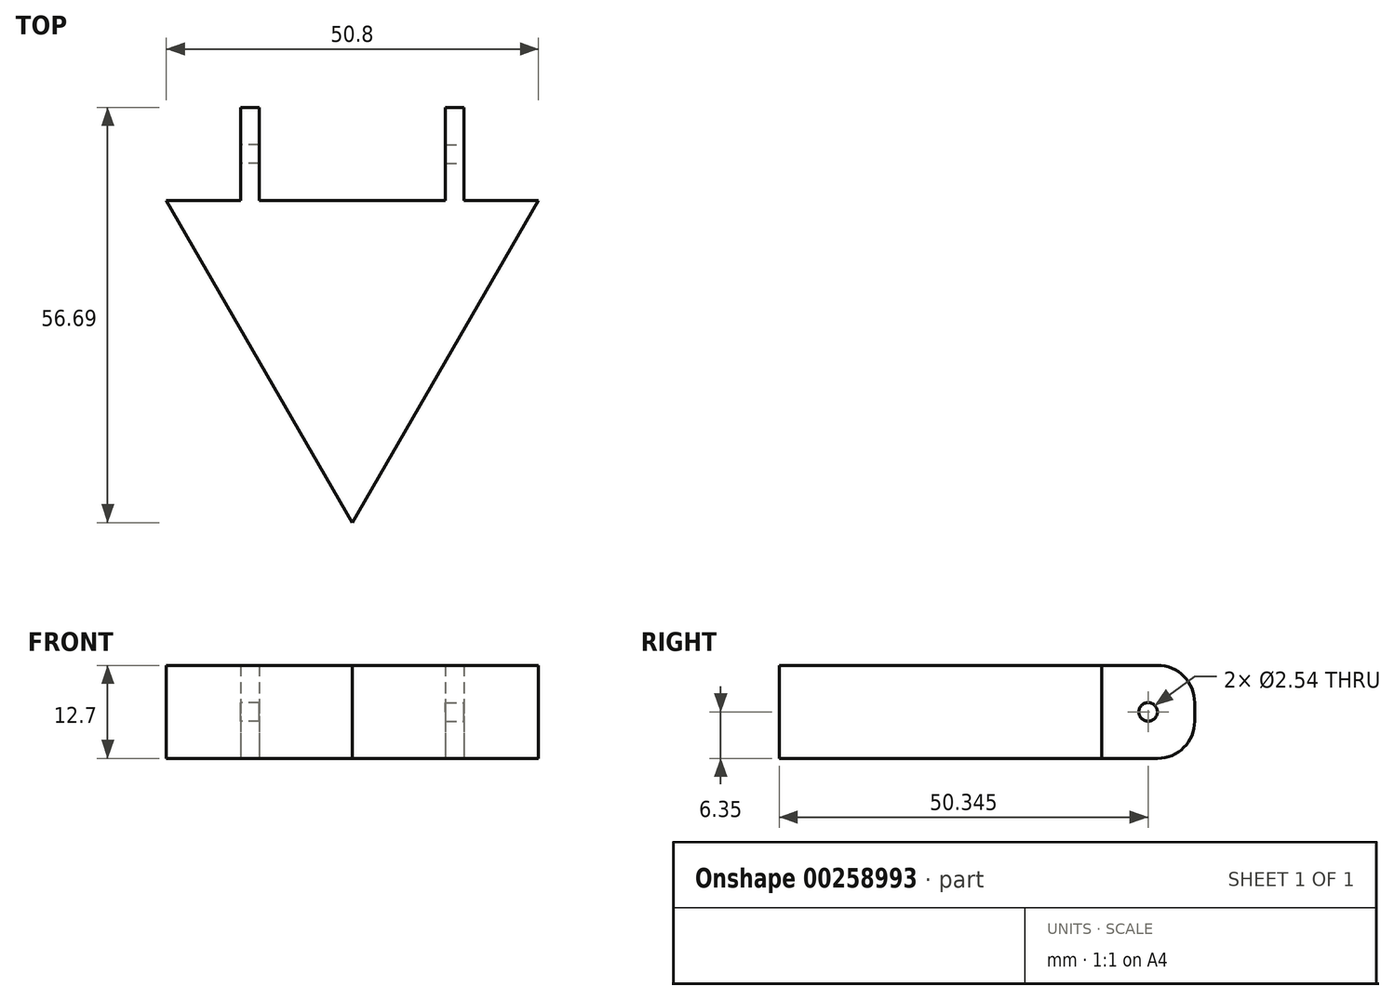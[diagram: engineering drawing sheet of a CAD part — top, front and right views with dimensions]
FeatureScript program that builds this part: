
annotation { "Feature Type Name" : "Feature", "Feature Type Description" : "" }
export const myFeature = defineFeature(function(context is Context, id is Id, definition is map)
    precondition{}
    {
        {
            var Q0;
            Q0=qCreatedBy(makeId("Top.planeOp"),FACE);
            var sketch = newSketch(context, id + "F0", { "sketchPlane" : qUnion([Q0])});
            skCircle(sketch, "E0.cCircle", {"center": v(0, 0) * mm, "radius": 14.66 * mm, "construction": true});
            skLineSegment(sketch, "E0.0", {"start": v(0, -29.33) * mm, "end": v(-25.4, 14.66) * mm});
            skLineSegment(sketch, "E0.1", {"start": v(-25.4, 14.66) * mm, "end": v(25.4, 14.66) * mm});
            skLineSegment(sketch, "E0.2", {"start": v(25.4, 14.66) * mm, "end": v(0, -29.33) * mm});
            skPoint(sketch, "E0.0.midPoint", {"position": v(-12.7, -7.33) * mm});
            skSolve(sketch);
        }
        {
            var Q0;
            Q0=makeQuery(id+"F0.imprint","IMPRINT",FACE,{"disambiguationData":[TD([[makeQuery(id+"F0.imprint","IMPRINT",EDGE,{"derivedFrom":sQuery(id+"F0.wireOp",EDGE,"E0.0")}),-1.0]])]});
            extrude(context, id + "F1", {"entities" : qUnion([Q0]), "depth" : 12.7 * mm});
        }
        {
            var Q0;
            Q0=makeQuery(id+"F1.opExtrude","SWEPT_FACE",FACE,{"disambiguationData":[OSD([sQuery(id+"F0.wireOp",EDGE,"E0.1")])]});
            var sketch = newSketch(context, id + "F2", { "sketchPlane" : qUnion([Q0])});
            skLineSegment(sketch, "E1", {"start": v(0, 12.7) * mm, "end": v(12.7, 12.7) * mm, "construction": true});
            skLineSegment(sketch, "E2", {"start": v(0, 12.7) * mm, "end": v(-12.7, 12.7) * mm, "construction": true});
            skLineSegment(sketch, "E3.bottom", {"start": v(-12.7, 12.7) * mm, "end": v(-15.24, 12.7) * mm});
            skLineSegment(sketch, "E3.top", {"start": v(-12.7, 0) * mm, "end": v(-15.24, 0) * mm});
            skLineSegment(sketch, "E3.left", {"start": v(-12.7, 12.7) * mm, "end": v(-12.7, 0) * mm});
            skLineSegment(sketch, "E3.right", {"start": v(-15.24, 12.7) * mm, "end": v(-15.24, 0) * mm});
            skLineSegment(sketch, "E4.bottom", {"start": v(12.7, 12.7) * mm, "end": v(15.24, 12.7) * mm});
            skLineSegment(sketch, "E4.top", {"start": v(12.7, 0) * mm, "end": v(15.24, 0) * mm});
            skLineSegment(sketch, "E4.left", {"start": v(12.7, 12.7) * mm, "end": v(12.7, 0) * mm});
            skLineSegment(sketch, "E4.right", {"start": v(15.24, 12.7) * mm, "end": v(15.24, 0) * mm});
            skSolve(sketch);
        }
        {
            var Q0;
            Q0=makeQuery(id+"F2.imprint","IMPRINT",FACE,{"disambiguationData":[TD([[makeQuery(id+"F2.imprint","IMPRINT",EDGE,{"derivedFrom":sQuery(id+"F2.wireOp",EDGE,"E3.bottom")}),1.0]])]});
            var Q1;
            Q1=makeQuery(id+"F2.imprint","IMPRINT",FACE,{"disambiguationData":[TD([[makeQuery(id+"F2.imprint","IMPRINT",EDGE,{"derivedFrom":sQuery(id+"F2.wireOp",EDGE,"E4.bottom")}),1.0]])]});
            extrude(context, id + "F3", {"entities" : qUnion([Q0, Q1]), "operationType" : NewBodyOperationType.ADD, "depth" : 12.7 * mm});
        }
        {
            var Q0;
            Q0=makeQuery(id+"F3.opExtrude","SWEPT_FACE",FACE,{"disambiguationData":[OSD([sQuery(id+"F2.wireOp",EDGE,"E3.right")])]});
            var sketch = newSketch(context, id + "F4", { "sketchPlane" : qUnion([Q0])});
            skLineSegment(sketch, "E5", {"start": v(27.36, 12.7) * mm, "end": v(14.66, 0) * mm, "construction": true});
            skLineSegment(sketch, "E6", {"start": v(27.36, 0) * mm, "end": v(14.66, 12.7) * mm, "construction": true});
            skCircle(sketch, "E7", {"center": v(21.01, 6.35) * mm, "radius": 1.27 * mm});
            skSolve(sketch);
        }
        {
            var Q0;
            Q0=makeQuery(id+"F4.imprint","IMPRINT",FACE,{"disambiguationData":[TD([[makeQuery(id+"F4.imprint","IMPRINT",EDGE,{"derivedFrom":sQuery(id+"F4.wireOp",EDGE,"E7")}),1.0]])]});
            extrude(context, id + "F5", {"entities" : qUnion([Q0]), "operationType" : NewBodyOperationType.REMOVE, "oppositeDirection" : true, "depth" : 25.4 * mm});
        }
        {
            var Q0;
            Q0=makeQuery(id+"F3.opExtrude","SWEPT_FACE",FACE,{"disambiguationData":[OSD([sQuery(id+"F2.wireOp",EDGE,"E4.right")])]});
            var sketch = newSketch(context, id + "F6", { "sketchPlane" : qUnion([Q0])});
            skLineSegment(sketch, "E8", {"start": v(-27.36, 12.7) * mm, "end": v(-14.66, 0) * mm, "construction": true});
            skLineSegment(sketch, "E9", {"start": v(-14.66, 12.7) * mm, "end": v(-27.36, 0) * mm, "construction": true});
            skCircle(sketch, "E10", {"center": v(-21.01, 6.35) * mm, "radius": 1.27 * mm});
            skSolve(sketch);
        }
        {
            var Q0;
            Q0=makeQuery(id+"F6.imprint","IMPRINT",FACE,{"disambiguationData":[TD([[makeQuery(id+"F6.imprint","IMPRINT",EDGE,{"derivedFrom":sQuery(id+"F6.wireOp",EDGE,"E10")}),1.0]])]});
            extrude(context, id + "F7", {"entities" : qUnion([Q0]), "operationType" : NewBodyOperationType.REMOVE, "oppositeDirection" : true, "depth" : 25.4 * mm});
        }
        {
            var Q0;
            Q0=makeQuery(id+"F3.opExtrude","CAP_EDGE",EDGE,{"disambiguationData":[OSD([sQuery(id+"F2.wireOp",EDGE,"E3.bottom")])],"isStart":false});
            var Q1;
            Q1=makeQuery(id+"F3.opExtrude","CAP_EDGE",EDGE,{"disambiguationData":[OSD([sQuery(id+"F2.wireOp",EDGE,"E3.top")])],"isStart":false});
            var Q2;
            Q2=makeQuery(id+"F3.opExtrude","CAP_EDGE",EDGE,{"disambiguationData":[OSD([sQuery(id+"F2.wireOp",EDGE,"E4.bottom")])],"isStart":false});
            var Q3;
            Q3=makeQuery(id+"F3.opExtrude","CAP_EDGE",EDGE,{"disambiguationData":[OSD([sQuery(id+"F2.wireOp",EDGE,"E4.top")])],"isStart":false});
            fillet(context, id + "F8", {"entities" : qUnion([Q0, Q1, Q2, Q3]), "radius" : 5.08 * mm, "tangentPropagation" : true, "allowEdgeOverflow" : false});
        }
    });
